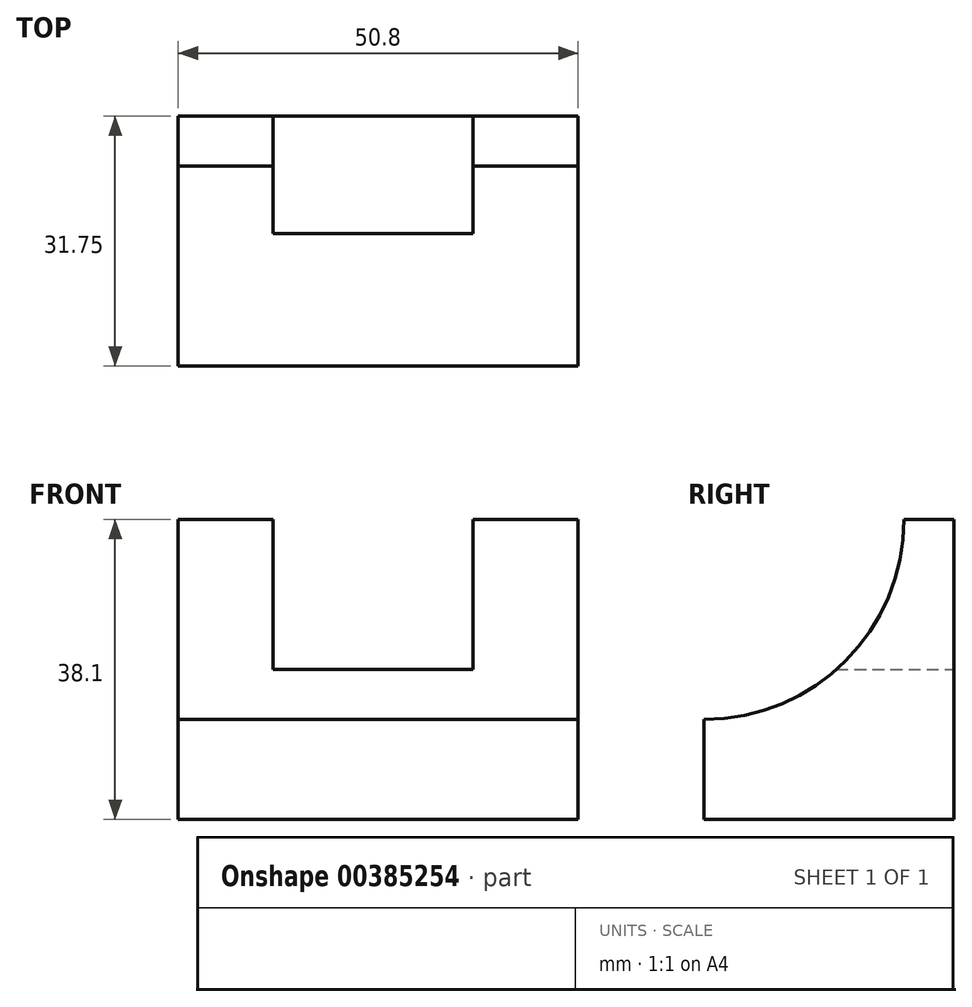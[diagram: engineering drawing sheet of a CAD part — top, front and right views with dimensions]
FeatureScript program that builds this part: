
annotation { "Feature Type Name" : "Feature", "Feature Type Description" : "" }
export const myFeature = defineFeature(function(context is Context, id is Id, definition is map)
    precondition{}
    {
        {
            var Q0;
            Q0=qCreatedBy(makeId("Front.planeOp"),FACE);
            var sketch = newSketch(context, id + "F0", { "sketchPlane" : qUnion([Q0])});
            skLineSegment(sketch, "E0.bottom", {"start": v(0, 0) * mm, "end": v(50.8, 0) * mm});
            skLineSegment(sketch, "E0.top", {"start": v(0, 38.1) * mm, "end": v(50.8, 38.1) * mm});
            skLineSegment(sketch, "E0.left", {"start": v(0, 0) * mm, "end": v(0, 38.1) * mm});
            skLineSegment(sketch, "E0.right", {"start": v(50.8, 0) * mm, "end": v(50.8, 38.1) * mm});
            skSolve(sketch);
        }
        {
            var Q0;
            Q0=qSketchRegion(id+"F0",true);
            extrude(context, id + "F1", {"entities" : qUnion([Q0]), "depth" : 31.75 * mm});
        }
        {
            var Q0;
            Q0=makeQuery(id+"F1.opExtrude","SWEPT_FACE",FACE,{"disambiguationData":[OSD([sQuery(id+"F0.wireOp",EDGE,"E0.right")])]});
            var sketch = newSketch(context, id + "F2", { "sketchPlane" : qUnion([Q0])});
            skArc(sketch, "E1", {"start": v(-31.75, 12.7) * mm, "mid": v(-13.79, 20.14) * mm, "end": v(-6.35, 38.1) * mm});
            skSolve(sketch);
        }
        {
            var Q0;
            {var subQ0=sQuery(id+"F2.wireOp",EDGE,"E1");Q0=makeQuery(id+"F2.imprint","IMPRINT",FACE,{"disambiguationData":[TD([[makeQuery(id+"F2.imprint","IMPRINT",EDGE,{"derivedFrom":subQ0}),1.0]])]});}
            extrude(context, id + "F3", {"entities" : qUnion([Q0]), "operationType" : NewBodyOperationType.REMOVE, "oppositeDirection" : true, "depth" : 50.8 * mm});
        }
        {
            var Q0;
            Q0=makeQuery(id+"F1.opExtrude","CAP_FACE",FACE,{"disambiguationData":[OSD([sQuery(id+"F0.wireOp",EDGE,"E0.bottom"),sQuery(id+"F0.wireOp",EDGE,"E0.top"),sQuery(id+"F0.wireOp",EDGE,"E0.left"),sQuery(id+"F0.wireOp",EDGE,"E0.right")])],"isStart":true});
            var sketch = newSketch(context, id + "F4", { "sketchPlane" : qUnion([Q0])});
            skLineSegment(sketch, "E2", {"start": v(-37.45, 38.1) * mm, "end": v(-37.45, 19.05) * mm});
            skLineSegment(sketch, "E3", {"start": v(-37.45, 19.05) * mm, "end": v(-12.05, 19.05) * mm});
            skLineSegment(sketch, "E4", {"start": v(-12.05, 19.05) * mm, "end": v(-12.05, 38.1) * mm});
            skSolve(sketch);
        }
        {
            var Q0;
            {var subQ0=sQuery(id+"F4.wireOp",EDGE,"E2");Q0=makeQuery(id+"F4.imprint","IMPRINT",FACE,{"disambiguationData":[TD([[makeQuery(id+"F4.imprint","IMPRINT",EDGE,{"derivedFrom":subQ0}),1.0]])]});}
            extrude(context, id + "F5", {"entities" : qUnion([Q0]), "operationType" : NewBodyOperationType.REMOVE, "oppositeDirection" : true, "depth" : 15.62 * mm});
        }
    });
